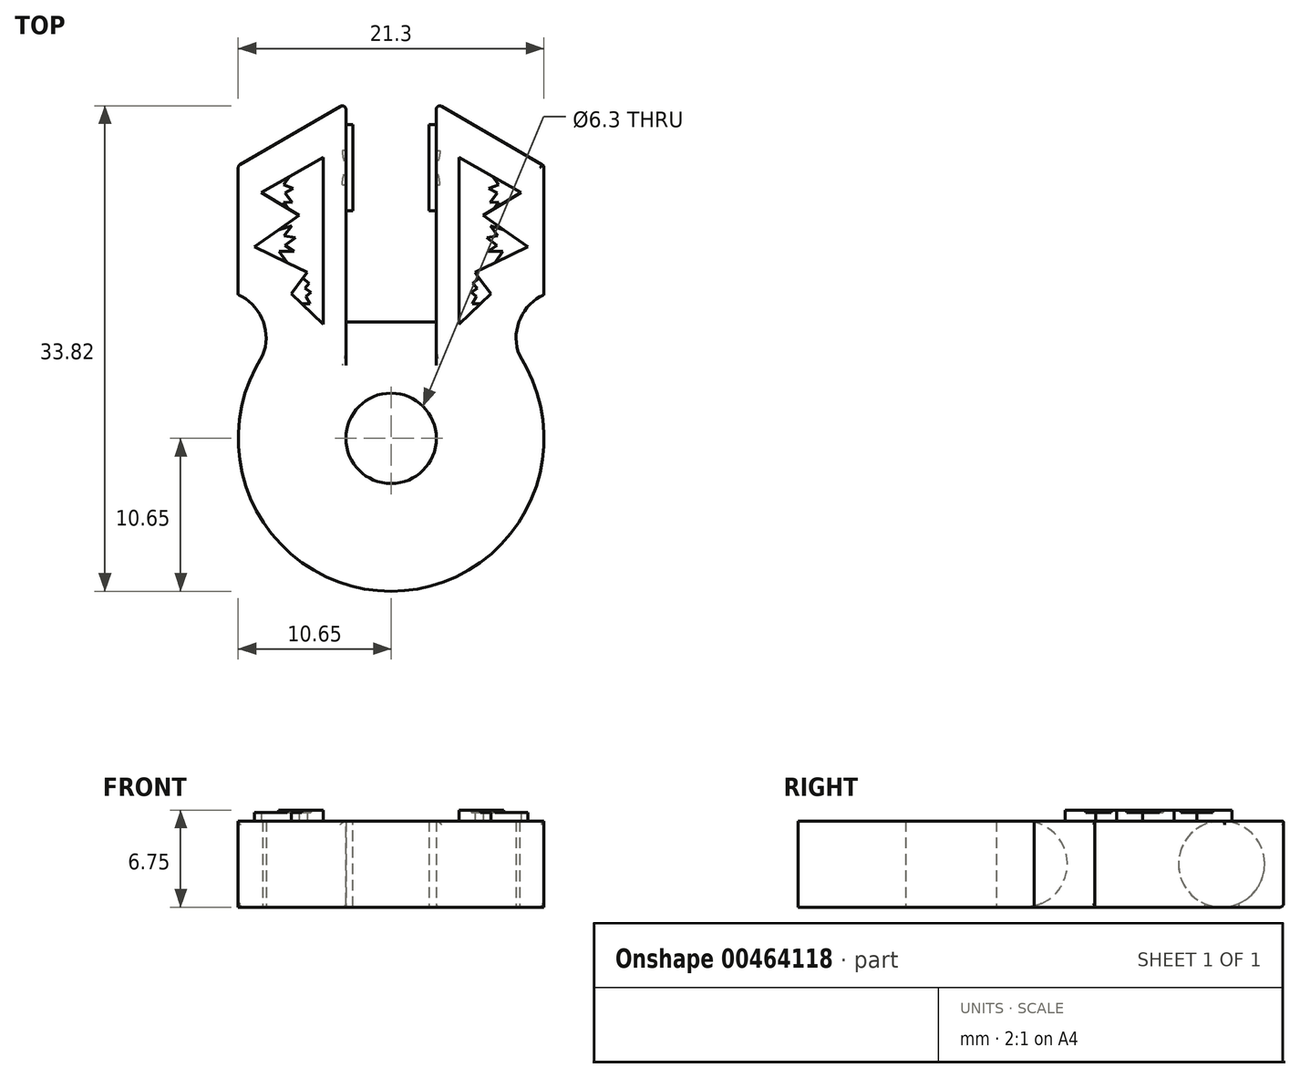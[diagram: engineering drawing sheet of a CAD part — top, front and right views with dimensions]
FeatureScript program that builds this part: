
annotation { "Feature Type Name" : "Feature", "Feature Type Description" : "" }
export const myFeature = defineFeature(function(context is Context, id is Id, definition is map)
    precondition{}
    {
        {
            var Q0;
            Q0=qCreatedBy(makeId("Top.planeOp"),FACE);
            var sketch = newSketch(context, id + "F0", { "sketchPlane" : qUnion([Q0])});
            skArc(sketch, "E0", {"start": v(-3.15, 10.17) * mm, "mid": v(0, -10.65) * mm, "end": v(3.15, 10.17) * mm});
            skCircle(sketch, "E1", {"center": v(0, 0) * mm, "radius": 3.15 * mm});
            skLineSegment(sketch, "E2", {"start": v(0, 0) * mm, "end": v(0, 3.15) * mm});
            skLineSegment(sketch, "E3", {"start": v(0, 8.1) * mm, "end": v(-3.15, 8.1) * mm});
            skLineSegment(sketch, "E4", {"start": v(-3.15, 8.1) * mm, "end": v(3.15, 8.1) * mm});
            skLineSegment(sketch, "E5", {"start": v(3.15, 8.1) * mm, "end": v(3.15, 23.35) * mm});
            skLineSegment(sketch, "E6", {"start": v(-3.15, 8.1) * mm, "end": v(-3.15, 23.35) * mm});
            skLineSegment(sketch, "E7", {"start": v(-10.65, 19) * mm, "end": v(-3.15, 23.35) * mm});
            skLineSegment(sketch, "E8", {"start": v(-10.65, 19) * mm, "end": v(-10.65, 10) * mm});
            skLineSegment(sketch, "E9.MirrorCS", {"start": v(10.65, 19) * mm, "end": v(10.65, 10) * mm});
            skLineSegment(sketch, "E10.MirrorCS", {"start": v(10.65, 19) * mm, "end": v(3.15, 23.35) * mm});
            skLineSegment(sketch, "E11", {"start": v(0, 0) * mm, "end": v(-12, 0) * mm});
            skArc(sketch, "E12", {"start": v(-10.65, 10) * mm, "mid": v(-8.95, 8.23) * mm, "end": v(-8.94, 5.78) * mm});
            skPoint(sketch, "E13.MirrorCS.end.orphan", {"position": v(10.65, 10) * mm});
            skArc(sketch, "E14.MirrorCS", {"start": v(10.65, 10) * mm, "mid": v(8.95, 8.23) * mm, "end": v(8.94, 5.78) * mm});
            skSolve(sketch);
        }
        {
            var Q0;
            Q0 = qSketchRegion(id + "F0", true);
            extrude(context, id + "F1", {"entities" : qUnion([Q0]), "depth" : 6 * mm});
        }
        {
            var Q0;
            Q0=makeQuery(id+"F1.opExtrude","SWEPT_FACE",FACE,{"disambiguationData":[OSD([sQuery(id+"F0.wireOp",EDGE,"E5")])]});
            var sketch = newSketch(context, id + "F2", { "sketchPlane" : qUnion([Q0])});
            skLineSegment(sketch, "E15", {"start": v(-23.35, 3) * mm, "end": v(-21.85, 3) * mm});
            skPoint(sketch, "E15.endSnap0", {"position": v(-23.35, 3) * mm});
            skLineSegment(sketch, "E16", {"start": v(-21.85, 3) * mm, "end": v(-18.85, 3) * mm});
            skCircle(sketch, "E17", {"center": v(-18.85, 3) * mm, "radius": 3 * mm});
            skSolve(sketch);
        }
        {
            var Q0;
            Q0 = qSketchRegion(id + "F2", true);
            extrude(context, id + "F3", {"entities" : qUnion([Q0]), "operationType" : NewBodyOperationType.ADD, "depth" : .5 * mm});
        }
        {
            var Q0;
            Q0=makeQuery(id+"F1.opExtrude","SWEPT_FACE",FACE,{"disambiguationData":[OSD([sQuery(id+"F0.wireOp",EDGE,"E6")])]});
            var sketch = newSketch(context, id + "F4", { "sketchPlane" : qUnion([Q0])});
            skLineSegment(sketch, "E18", {"start": v(23.35, 3) * mm, "end": v(18.85, 3) * mm});
            skCircle(sketch, "E19", {"center": v(18.85, 3) * mm, "radius": 3 * mm});
            skSolve(sketch);
        }
        {
            var Q0;
            Q0 = qSketchRegion(id + "F4", true);
            extrude(context, id + "F5", {"entities" : qUnion([Q0]), "operationType" : NewBodyOperationType.ADD, "depth" : .5 * mm});
        }
        {
            var Q0;
            {var subQ0=sQuery(id+"F0.wireOp",EDGE,"E4");var subQ7=sQuery(id+"F0.wireOp",EDGE,"E6");var subQ11=makeQuery(id+"F1.opExtrude","SWEPT_FACE",FACE,{"disambiguationData":[OSD([subQ7])]});Q0=makeQuery(id+"F5.boolean.opBoolean","SPLIT",FACE,{"disambiguationData":[TD([makeQuery(id+"F1.opExtrude","SWEPT_FACE",FACE,{"disambiguationData":[OSD([subQ0])]})])],"derivedFrom":subQ11});}
            var sketch = newSketch(context, id + "F6", { "sketchPlane" : qUnion([Q0])});
            skLineSegment(sketch, "E20.bottom", {"start": v(8.1, 6) * mm, "end": v(5.1, 6) * mm});
            skLineSegment(sketch, "E20.top", {"start": v(8.1, 0) * mm, "end": v(5.1, 0) * mm});
            skLineSegment(sketch, "E20.left", {"start": v(8.1, 6) * mm, "end": v(8.1, 0) * mm});
            skArc(sketch, "E21", {"start": v(5.1, 0) * mm, "mid": v(8.1, 3) * mm, "end": v(5.1, 6) * mm});
            skSolve(sketch);
        }
        {
            var Q0;
            Q0 = qSketchRegion(id + "F6", true);
            extrude(context, id + "F7", {"entities" : qUnion([Q0]), "operationType" : NewBodyOperationType.REMOVE, "depth" : 6.3 * mm});
        }
        {
            var Q0;
            Q0=makeQuery(id+"F1.opExtrude","CAP_FACE",FACE,{"disambiguationData":[OSD([sQuery(id+"F0.wireOp",EDGE,"E0"),sQuery(id+"F0.wireOp",EDGE,"E1"),sQuery(id+"F0.wireOp",EDGE,"E4"),sQuery(id+"F0.wireOp",EDGE,"E5"),sQuery(id+"F0.wireOp",EDGE,"E6"),sQuery(id+"F0.wireOp",EDGE,"E7"),sQuery(id+"F0.wireOp",EDGE,"E8"),sQuery(id+"F0.wireOp",EDGE,"E9.MirrorCS"),sQuery(id+"F0.wireOp",EDGE,"E10.MirrorCS"),sQuery(id+"F0.wireOp",EDGE,"E12"),sQuery(id+"F0.wireOp",EDGE,"E14.MirrorCS")])],"isStart":false});
            var sketch = newSketch(context, id + "F8", { "sketchPlane" : qUnion([Q0])});
            skLineSegment(sketch, "E22", {"start": v(-4.73, 19.57) * mm, "end": v(-9.05, 17.13) * mm});
            skLineSegment(sketch, "E23", {"start": v(-9.05, 17.13) * mm, "end": v(-5.38, 14.9) * mm});
            skLineSegment(sketch, "E24", {"start": v(-6.4, 15.52) * mm, "end": v(-9.51, 13.35) * mm});
            skLineSegment(sketch, "E25", {"start": v(-9.51, 13.35) * mm, "end": v(-5.84, 11.55) * mm});
            skLineSegment(sketch, "E26", {"start": v(-4.73, 13.02) * mm, "end": v(-6.96, 10.07) * mm});
            skLineSegment(sketch, "E27", {"start": v(-6.96, 10.07) * mm, "end": v(-4.73, 7.95) * mm});
            skLineSegment(sketch, "E28", {"start": v(-4.73, 7.95) * mm, "end": v(-4.73, 19.57) * mm});
            skPoint(sketch, "E29.orphan", {"position": v(-4.73, 11) * mm});
            skLineSegment(sketch, "E30", {"start": v(-5.38, 14.9) * mm, "end": v(-4.73, 14.4) * mm});
            skLineSegment(sketch, "E31", {"start": v(-7.08, 18.24) * mm, "end": v(-7.5, 17.65) * mm});
            skLineSegment(sketch, "E32", {"start": v(-7.5, 17.65) * mm, "end": v(-6.8, 17.41) * mm});
            skLineSegment(sketch, "E33", {"start": v(-6.8, 17.41) * mm, "end": v(-7.4, 17.08) * mm});
            skLineSegment(sketch, "E34", {"start": v(-7.4, 17.08) * mm, "end": v(-6.9, 16.41) * mm});
            skLineSegment(sketch, "E35", {"start": v(-6.9, 16.41) * mm, "end": v(-7.5, 16.46) * mm});
            skLineSegment(sketch, "E36", {"start": v(-7.5, 16.46) * mm, "end": v(-7.21, 16.01) * mm});
            skLineSegment(sketch, "E37", {"start": v(-7.83, 14.53) * mm, "end": v(-6.93, 14.8) * mm});
            skLineSegment(sketch, "E38", {"start": v(-6.93, 14.8) * mm, "end": v(-7.44, 14.1) * mm});
            skLineSegment(sketch, "E39", {"start": v(-7.44, 14.1) * mm, "end": v(-6.67, 13.98) * mm});
            skLineSegment(sketch, "E40", {"start": v(-6.67, 13.98) * mm, "end": v(-7.38, 13.43) * mm});
            skLineSegment(sketch, "E41", {"start": v(-7.38, 13.43) * mm, "end": v(-6.76, 13.02) * mm});
            skLineSegment(sketch, "E42", {"start": v(-6.76, 13.02) * mm, "end": v(-7.8, 13.02) * mm});
            skLineSegment(sketch, "E43", {"start": v(-7.8, 13.02) * mm, "end": v(-7.24, 12.24) * mm});
            skLineSegment(sketch, "E44", {"start": v(-6.14, 11.15) * mm, "end": v(-5.7, 10.82) * mm});
            skLineSegment(sketch, "E45", {"start": v(-5.7, 10.82) * mm, "end": v(-5.99, 10.47) * mm});
            skLineSegment(sketch, "E46", {"start": v(-5.99, 10.47) * mm, "end": v(-5.58, 10.16) * mm});
            skLineSegment(sketch, "E47", {"start": v(-5.58, 10.16) * mm, "end": v(-5.93, 9.87) * mm});
            skLineSegment(sketch, "E48", {"start": v(-5.93, 9.87) * mm, "end": v(-5.65, 9.38) * mm});
            skLineSegment(sketch, "E49", {"start": v(-5.65, 9.38) * mm, "end": v(-6.23, 9.38) * mm});
            skSolve(sketch);
        }
        {
            var Q0;
            Q0=makeQuery(id+"F1.opExtrude","SWEPT_EDGE",EDGE,{"disambiguationData":[OSD([sQuery(id+"F0.wireOp",EDGE,"E7"),sQuery(id+"F0.wireOp",EDGE,"E8")])]});
            var Q1;
            Q1=makeQuery(id+"F1.opExtrude","CAP_EDGE",EDGE,{"disambiguationData":[OSD([sQuery(id+"F0.wireOp",EDGE,"E8")])],"isStart":true});
            var Q2;
            Q2=makeQuery(id+"F1.opExtrude","CAP_EDGE",EDGE,{"disambiguationData":[OSD([sQuery(id+"F0.wireOp",EDGE,"E8")])],"isStart":false});
            var Q3;
            Q3=makeQuery(id+"F1.opExtrude","CAP_EDGE",EDGE,{"disambiguationData":[OSD([sQuery(id+"F0.wireOp",EDGE,"E7")])],"isStart":false});
            var Q4;
            Q4=makeQuery(id+"F1.opExtrude","CAP_EDGE",EDGE,{"disambiguationData":[OSD([sQuery(id+"F0.wireOp",EDGE,"E12")])],"isStart":false});
            var Q5;
            Q5=makeQuery(id+"F1.opExtrude","CAP_EDGE",EDGE,{"disambiguationData":[OSD([sQuery(id+"F0.wireOp",EDGE,"E12")])],"isStart":true});
            var Q6;
            Q6=makeQuery(id+"F1.opExtrude","CAP_EDGE",EDGE,{"disambiguationData":[OSD([sQuery(id+"F0.wireOp",EDGE,"E9.MirrorCS")])],"isStart":true});
            var Q7;
            Q7=makeQuery(id+"F1.opExtrude","CAP_EDGE",EDGE,{"disambiguationData":[OSD([sQuery(id+"F0.wireOp",EDGE,"E9.MirrorCS")])],"isStart":false});
            var Q8;
            Q8=makeQuery(id+"F1.opExtrude","SWEPT_EDGE",EDGE,{"disambiguationData":[OSD([sQuery(id+"F0.wireOp",EDGE,"E9.MirrorCS"),sQuery(id+"F0.wireOp",EDGE,"E14.MirrorCS")])]});
            var Q9;
            Q9=makeQuery(id+"F1.opExtrude","SWEPT_EDGE",EDGE,{"disambiguationData":[OSD([sQuery(id+"F0.wireOp",EDGE,"E9.MirrorCS"),sQuery(id+"F0.wireOp",EDGE,"E10.MirrorCS")])]});
            var Q10;
            Q10=makeQuery(id+"F1.opExtrude","CAP_EDGE",EDGE,{"disambiguationData":[OSD([sQuery(id+"F0.wireOp",EDGE,"E10.MirrorCS")])],"isStart":false});
            var Q11;
            Q11=makeQuery(id+"F1.opExtrude","CAP_EDGE",EDGE,{"disambiguationData":[OSD([sQuery(id+"F0.wireOp",EDGE,"E10.MirrorCS")])],"isStart":true});
            var Q12;
            Q12=makeQuery(id+"F1.opExtrude","SWEPT_EDGE",EDGE,{"disambiguationData":[OSD([sQuery(id+"F0.wireOp",EDGE,"E5"),sQuery(id+"F0.wireOp",EDGE,"E10.MirrorCS")])]});
            var Q13;
            Q13=makeQuery(id+"F1.opExtrude","SWEPT_EDGE",EDGE,{"disambiguationData":[OSD([sQuery(id+"F0.wireOp",EDGE,"E6"),sQuery(id+"F0.wireOp",EDGE,"E7")])]});
            var Q14;
            Q14=makeQuery(id+"F1.opExtrude","CAP_EDGE",EDGE,{"disambiguationData":[OSD([sQuery(id+"F0.wireOp",EDGE,"E7")])],"isStart":true});
            var Q15;
            {var subQ0=sQuery(id+"F0.wireOp",EDGE,"E6");var subQ1=sQuery(id+"F0.wireOp",EDGE,"E4");Q15=makeQuery(id+"F7.boolean.opBoolean","MERGE",EDGE,{"derivedFrom":[makeQuery(id+"F5.boolean.opBoolean","SPLIT",EDGE,{"disambiguationData":[TD([makeQuery(id+"F1.opExtrude","SWEPT_FACE",FACE,{"disambiguationData":[OSD([subQ1])]})])],"derivedFrom":makeQuery(id+"F1.opExtrude","CAP_EDGE",EDGE,{"disambiguationData":[OSD([subQ0])],"isStart":true})}),makeQuery(id+"F7.opExtrude","CAP_EDGE",EDGE,{"disambiguationData":[OSD([sQuery(id+"F6.wireOp",EDGE,"E20.top")])],"isStart":true})]});}
            var Q16;
            {var subQ0=sQuery(id+"F0.wireOp",EDGE,"E5");var subQ1=sQuery(id+"F0.wireOp",EDGE,"E4");Q16=makeQuery(id+"F7.boolean.opBoolean","MERGE",EDGE,{"derivedFrom":[makeQuery(id+"F3.boolean.opBoolean","SPLIT",EDGE,{"disambiguationData":[TD([makeQuery(id+"F1.opExtrude","SWEPT_FACE",FACE,{"disambiguationData":[OSD([subQ1])]})])],"derivedFrom":makeQuery(id+"F1.opExtrude","CAP_EDGE",EDGE,{"disambiguationData":[OSD([subQ0])],"isStart":false})}),makeQuery(id+"F7.opExtrude","CAP_EDGE",EDGE,{"disambiguationData":[OSD([sQuery(id+"F6.wireOp",EDGE,"E20.bottom")])],"isStart":false})]});}
            var Q17;
            {var subQ0=sQuery(id+"F0.wireOp",EDGE,"E6");var subQ1=sQuery(id+"F0.wireOp",EDGE,"E4");Q17=makeQuery(id+"F7.boolean.opBoolean","MERGE",EDGE,{"derivedFrom":[makeQuery(id+"F5.boolean.opBoolean","SPLIT",EDGE,{"disambiguationData":[TD([makeQuery(id+"F1.opExtrude","SWEPT_FACE",FACE,{"disambiguationData":[OSD([subQ1])]})])],"derivedFrom":makeQuery(id+"F1.opExtrude","CAP_EDGE",EDGE,{"disambiguationData":[OSD([subQ0])],"isStart":false})}),makeQuery(id+"F7.opExtrude","CAP_EDGE",EDGE,{"disambiguationData":[OSD([sQuery(id+"F6.wireOp",EDGE,"E20.bottom")])],"isStart":true})]});}
            var Q18;
            {var subQ0=sQuery(id+"F0.wireOp",EDGE,"E5");var subQ1=sQuery(id+"F0.wireOp",EDGE,"E4");Q18=makeQuery(id+"F7.boolean.opBoolean","MERGE",EDGE,{"derivedFrom":[makeQuery(id+"F3.boolean.opBoolean","SPLIT",EDGE,{"disambiguationData":[TD([makeQuery(id+"F1.opExtrude","SWEPT_FACE",FACE,{"disambiguationData":[OSD([subQ1])]})])],"derivedFrom":makeQuery(id+"F1.opExtrude","CAP_EDGE",EDGE,{"disambiguationData":[OSD([subQ0])],"isStart":true})}),makeQuery(id+"F7.opExtrude","CAP_EDGE",EDGE,{"disambiguationData":[OSD([sQuery(id+"F6.wireOp",EDGE,"E20.top")])],"isStart":false})]});}
            var Q19;
            {var subQ0=sQuery(id+"F0.wireOp",EDGE,"E7");var subQ1=sQuery(id+"F0.wireOp",EDGE,"E6");Q19=makeQuery(id+"F5.boolean.opBoolean","SPLIT",EDGE,{"disambiguationData":[TD([makeQuery(id+"F1.opExtrude","SWEPT_FACE",FACE,{"disambiguationData":[OSD([subQ0])]})])],"derivedFrom":makeQuery(id+"F1.opExtrude","CAP_EDGE",EDGE,{"disambiguationData":[OSD([subQ1])],"isStart":true})});}
            var Q20;
            {var subQ0=sQuery(id+"F0.wireOp",EDGE,"E10.MirrorCS");var subQ1=sQuery(id+"F0.wireOp",EDGE,"E5");Q20=makeQuery(id+"F3.boolean.opBoolean","SPLIT",EDGE,{"disambiguationData":[TD([makeQuery(id+"F1.opExtrude","SWEPT_FACE",FACE,{"disambiguationData":[OSD([subQ0])]})])],"derivedFrom":makeQuery(id+"F1.opExtrude","CAP_EDGE",EDGE,{"disambiguationData":[OSD([subQ1])],"isStart":true})});}
            var Q21;
            {var subQ0=sQuery(id+"F0.wireOp",EDGE,"E7");var subQ1=sQuery(id+"F0.wireOp",EDGE,"E6");Q21=makeQuery(id+"F5.boolean.opBoolean","SPLIT",EDGE,{"disambiguationData":[TD([makeQuery(id+"F1.opExtrude","SWEPT_FACE",FACE,{"disambiguationData":[OSD([subQ0])]})])],"derivedFrom":makeQuery(id+"F1.opExtrude","CAP_EDGE",EDGE,{"disambiguationData":[OSD([subQ1])],"isStart":false})});}
            fillet(context, id + "F9", {"entities" : qUnion([Q0, Q1, Q2, Q3, Q4, Q5, Q6, Q7, Q8, Q9, Q10, Q11, Q12, Q13, Q14, Q15, Q16, Q17, Q18, Q19, Q20, Q21]), "radius" : .25 * mm, "tangentPropagation" : true, "allowEdgeOverflow" : false});
        }
        {
            var Q0;
            {var subQ6=sQuery(id+"F8.wireOp",EDGE,"E44");Q0=makeQuery(id+"F8.imprint","IMPRINT",FACE,{"disambiguationData":[TD([[makeQuery(id+"F8.imprint","IMPRINT",EDGE,{"derivedFrom":subQ6}),1.0]])]});}
            var Q1;
            {var subQ1=sQuery(id+"F8.wireOp",EDGE,"E30");Q1=makeQuery(id+"F8.imprint","IMPRINT",FACE,{"disambiguationData":[TD([[makeQuery(id+"F8.imprint","IMPRINT",EDGE,{"derivedFrom":subQ1}),-1.0]])]});}
            var Q2;
            {var subQ1=sQuery(id+"F8.wireOp",EDGE,"E30");Q2=makeQuery(id+"F8.imprint","IMPRINT",FACE,{"disambiguationData":[TD([[makeQuery(id+"F8.imprint","IMPRINT",EDGE,{"derivedFrom":subQ1}),1.0]])]});}
            extrude(context, id + "F10", {"entities" : qUnion([Q0, Q1, Q2]), "operationType" : NewBodyOperationType.ADD, "depth" : .75 * mm});
        }
        {
            var Q0;
            {var subQ4=sQuery(id+"F8.wireOp",EDGE,"E44");Q0=makeQuery(id+"F8.imprint","IMPRINT",FACE,{"disambiguationData":[TD([[makeQuery(id+"F8.imprint","IMPRINT",EDGE,{"derivedFrom":subQ4}),-1.0]])]});}
            var Q1;
            {var subQ0=sQuery(id+"F8.wireOp",EDGE,"E37");Q1=makeQuery(id+"F8.imprint","IMPRINT",FACE,{"disambiguationData":[TD([[makeQuery(id+"F8.imprint","IMPRINT",EDGE,{"derivedFrom":subQ0}),-1.0]])]});}
            var Q2;
            {var subQ0=sQuery(id+"F8.wireOp",EDGE,"E31");Q2=makeQuery(id+"F8.imprint","IMPRINT",FACE,{"disambiguationData":[TD([[makeQuery(id+"F8.imprint","IMPRINT",EDGE,{"derivedFrom":subQ0}),-1.0]])]});}
            extrude(context, id + "F11", {"entities" : qUnion([Q0, Q1, Q2]), "operationType" : NewBodyOperationType.ADD, "depth" : .6 * mm});
        }
        {
            var Q0;
            Q0=makeQuery(id+"F1.opExtrude","SWEPT_BODY",BODY,{"disambiguationData":[OSD([sQuery(id+"F0.wireOp",EDGE,"E0"),sQuery(id+"F0.wireOp",EDGE,"E1"),sQuery(id+"F0.wireOp",EDGE,"E4"),sQuery(id+"F0.wireOp",EDGE,"E5"),sQuery(id+"F0.wireOp",EDGE,"E6"),sQuery(id+"F0.wireOp",EDGE,"E7"),sQuery(id+"F0.wireOp",EDGE,"E8"),sQuery(id+"F0.wireOp",EDGE,"E9.MirrorCS"),sQuery(id+"F0.wireOp",EDGE,"E10.MirrorCS"),sQuery(id+"F0.wireOp",EDGE,"E12"),sQuery(id+"F0.wireOp",EDGE,"E14.MirrorCS")])]});
            var Q1;
            Q1=qCreatedBy(makeId("Right.planeOp"),FACE);
            mirror(context, id + "F12", {"operationType" : NewBodyOperationType.ADD, "entities" : qUnion([Q0]), "mirrorPlane" : qUnion([Q1])});
        }
    });
